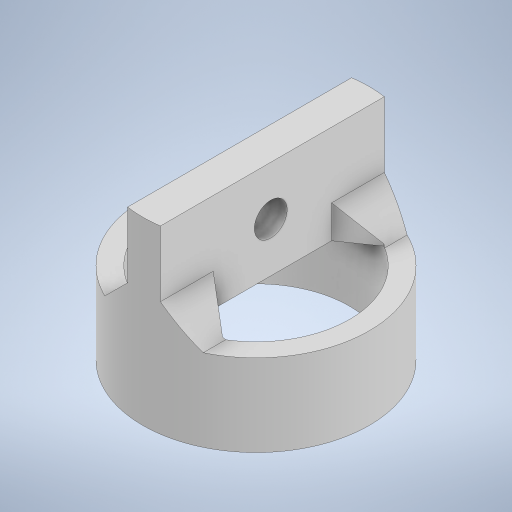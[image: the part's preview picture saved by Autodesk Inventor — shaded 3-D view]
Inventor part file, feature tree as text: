
AUTODESK INVENTOR PART (.ipt)
format: ipt  version: 2024 (Build 280153000, 153)  size: 266,240 bytes
history: native  units: mm
features: extrude x3, chamfer x2, other x1, sketch x1, projected_geometry x1
ambient origin geometry x8: Origin, YZ Plane, XZ Plane, XY Plane, X Axis, Y Axis, Z Axis, Center Point
bodies: Body1 (feature_tree)
feature tree (8):
  other  "솔리드1"
  extrude  "돌출1"  Depth=5.7mm
  extrude  "돌출2"  Depth=6.9mm
  chamfer  "모따기1"  Distance=2.5mm
  chamfer  "모따기2"  Distance=1.0mm
  extrude  "돌출4"  Depth=3.0mm TaperAngle=0.0deg
  sketch  "스케치5"
  projected_geometry  "투영된 루프3"
